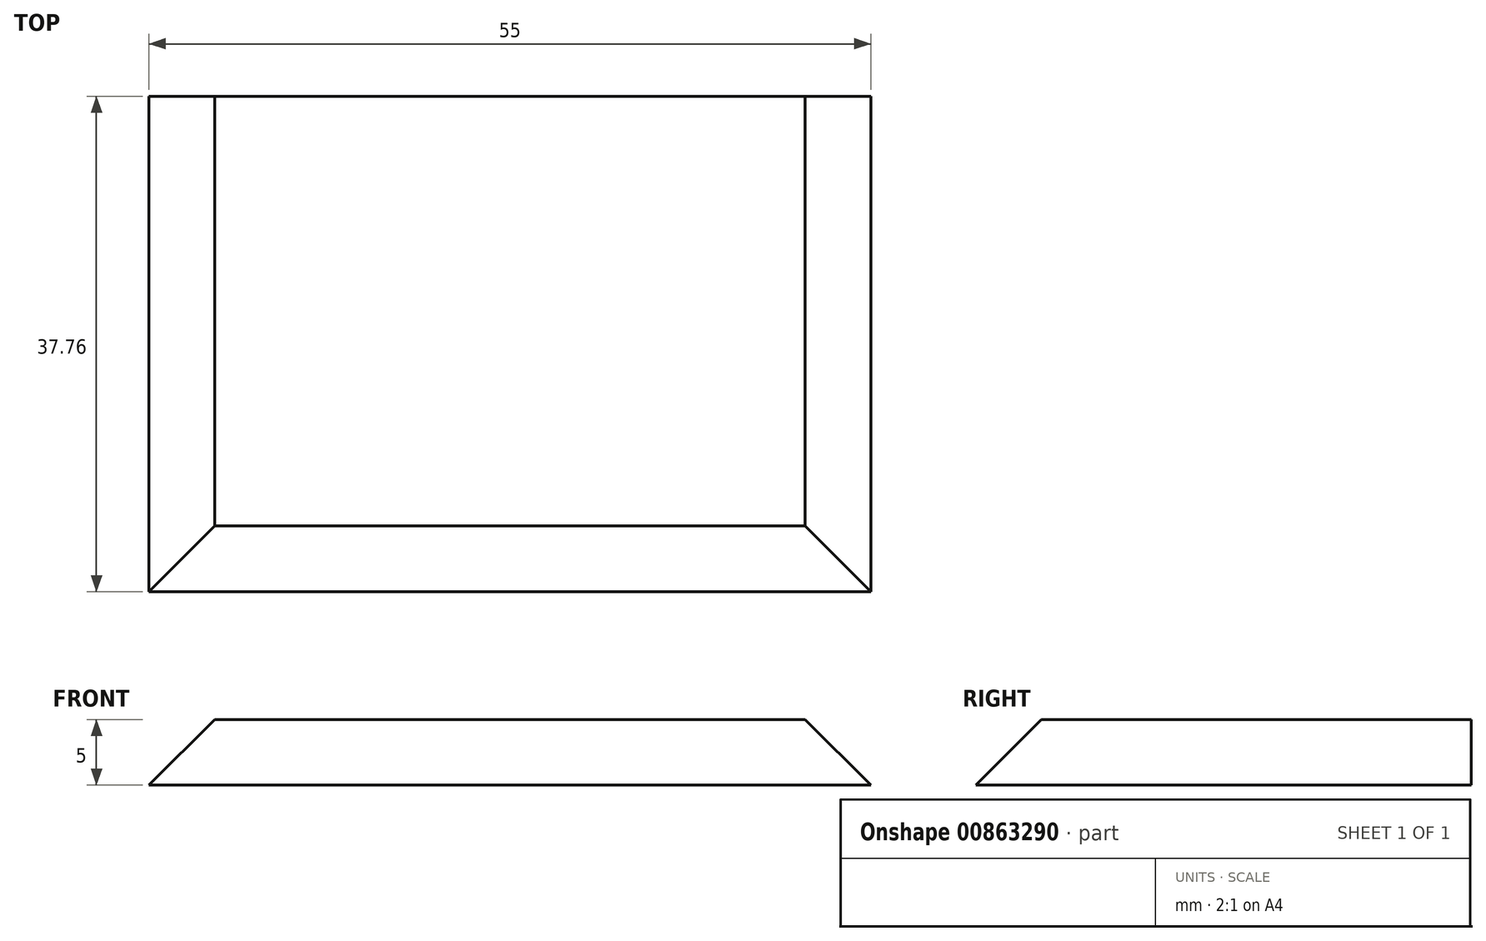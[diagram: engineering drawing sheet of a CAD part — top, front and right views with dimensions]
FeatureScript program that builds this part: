
annotation { "Feature Type Name" : "Feature", "Feature Type Description" : "" }
export const myFeature = defineFeature(function(context is Context, id is Id, definition is map)
    precondition{}
    {
        {
            var Q0;
            Q0=qCreatedBy(makeId("Top.planeOp"),FACE);
            var sketch = newSketch(context, id + "F0", { "sketchPlane" : qUnion([Q0])});
            skLineSegment(sketch, "E0.bottom", {"start": v(27.5, -52.5) * mm, "end": v(-27.5, -52.5) * mm});
            skLineSegment(sketch, "E0.top", {"start": v(27.5, 52.5) * mm, "end": v(-27.5, 52.5) * mm});
            skLineSegment(sketch, "E0.left", {"start": v(27.5, -52.5) * mm, "end": v(27.5, 52.5) * mm});
            skLineSegment(sketch, "E0.right", {"start": v(-27.5, -52.5) * mm, "end": v(-27.5, 52.5) * mm});
            skPoint(sketch, "E0.middle", {"position": v(0, 0) * mm});
            skLineSegment(sketch, "E1", {"start": v(27.5, -14.74) * mm, "end": v(-27.5, -11.5) * mm});
            skLineSegment(sketch, "E2", {"start": v(27.5, -14.74) * mm, "end": v(-27.5, -14.74) * mm});
            skSolve(sketch);
        }
        {
            var Q0;
            {var subQ0=sQuery(id+"F0.wireOp",EDGE,"E0.bottom");Q0=makeQuery(id+"F0.imprint","IMPRINT",FACE,{"disambiguationData":[TD([[makeQuery(id+"F0.imprint","IMPRINT",EDGE,{"derivedFrom":subQ0}),-1.0]])]});}
            extrude(context, id + "F1", {"entities" : qUnion([Q0]), "depth" : 5 * mm, "offsetDistance" : 25 * mm});
        }
        {
            var Q0;
            Q0=makeQuery(id+"F1.opExtrude","CAP_EDGE",EDGE,{"disambiguationData":[OSD([sQuery(id+"F0.wireOp",EDGE,"E0.top")])],"isStart":true});
            var Q1;
            Q1=makeQuery(id+"F1.opExtrude","CAP_EDGE",EDGE,{"disambiguationData":[OSD([sQuery(id+"F0.wireOp",EDGE,"E0.right")])],"isStart":false});
            var Q2;
            Q2=makeQuery(id+"F1.opExtrude","CAP_EDGE",EDGE,{"disambiguationData":[OSD([sQuery(id+"F0.wireOp",EDGE,"E0.left")])],"isStart":false});
            var Q3;
            Q3=makeQuery(id+"F1.opExtrude","CAP_EDGE",EDGE,{"disambiguationData":[OSD([sQuery(id+"F0.wireOp",EDGE,"E0.bottom")])],"isStart":false});
            chamfer(context, id + "F2", {"entities" : qUnion([Q0, Q1, Q2, Q3]), "width" : 5 * mm, "tangentPropagation" : true});
        }
    });
